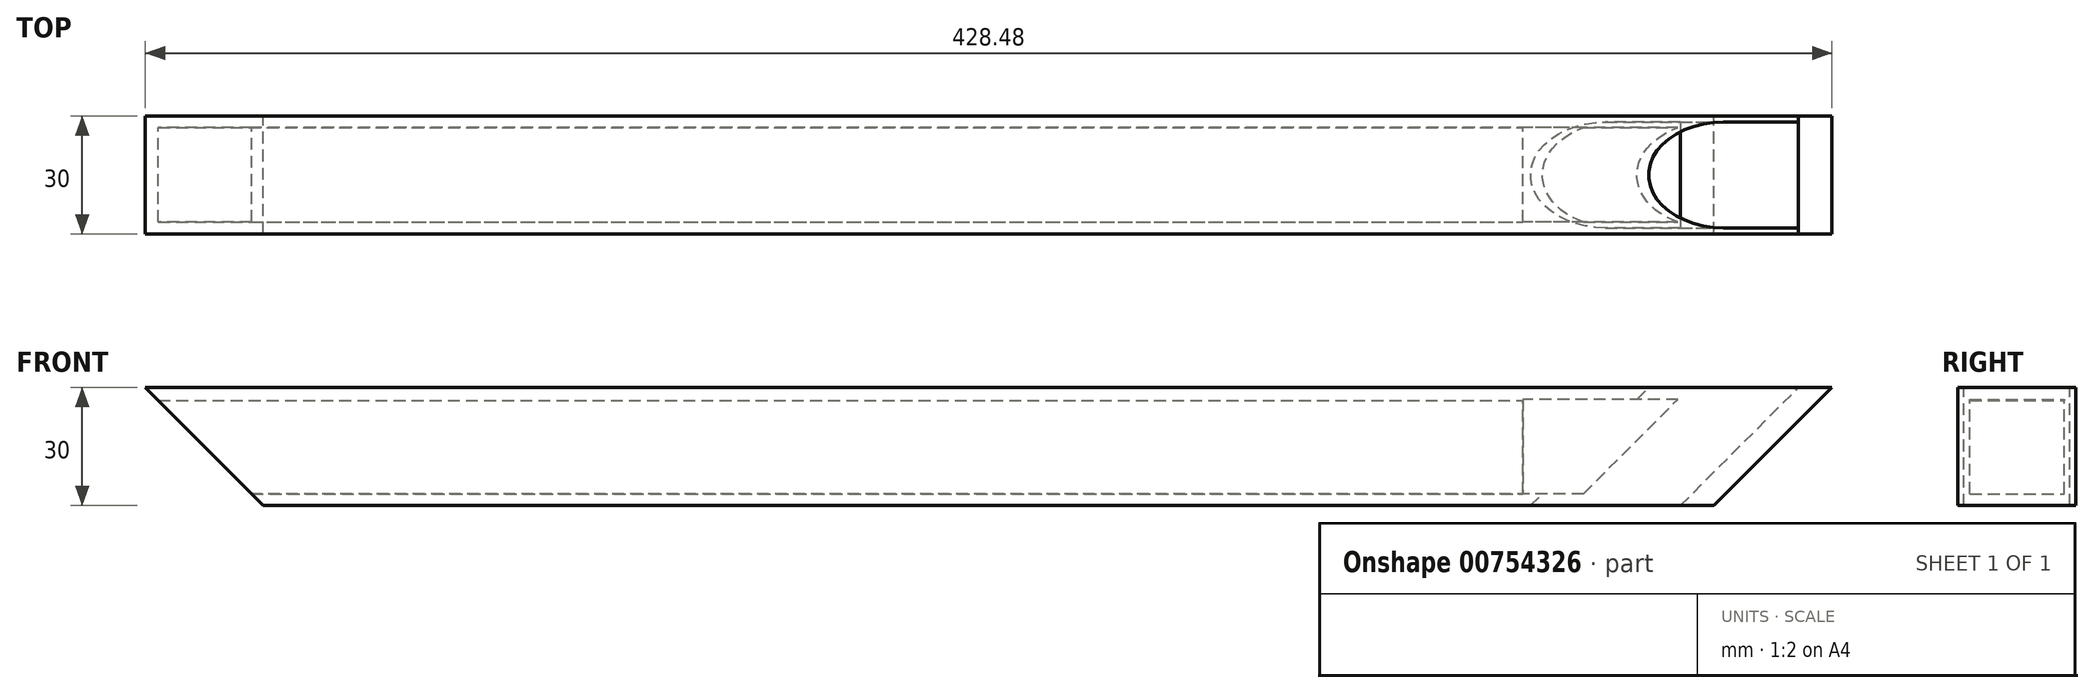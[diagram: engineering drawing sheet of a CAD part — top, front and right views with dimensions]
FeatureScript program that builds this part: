
annotation { "Feature Type Name" : "Feature", "Feature Type Description" : "" }
export const myFeature = defineFeature(function(context is Context, id is Id, definition is map)
    precondition{}
    {
        {
            var Q0;
            Q0=qCreatedBy(makeId("Right.planeOp"),FACE);
            var sketch = newSketch(context, id + "F0", { "sketchPlane" : qUnion([Q0])});
            skLineSegment(sketch, "E0.bottom", {"start": v(15, 15) * mm, "end": v(-15, 15) * mm});
            skLineSegment(sketch, "E0.top", {"start": v(15, -15) * mm, "end": v(-15, -15) * mm});
            skLineSegment(sketch, "E0.left", {"start": v(15, 15) * mm, "end": v(15, -15) * mm});
            skLineSegment(sketch, "E0.right", {"start": v(-15, 15) * mm, "end": v(-15, -15) * mm});
            skPoint(sketch, "E0.middle", {"position": v(0, 0) * mm});
            skLineSegment(sketch, "E1.bottom", {"start": v(12, -12) * mm, "end": v(-12, -12) * mm});
            skLineSegment(sketch, "E1.top", {"start": v(12, 12) * mm, "end": v(-12, 12) * mm});
            skLineSegment(sketch, "E1.left", {"start": v(12, -12) * mm, "end": v(12, 12) * mm});
            skLineSegment(sketch, "E1.right", {"start": v(-12, -12) * mm, "end": v(-12, 12) * mm});
            skLineSegment(sketch, "E2", {"start": v(12, 0) * mm, "end": v(15, 0) * mm, "construction": true});
            skLineSegment(sketch, "E3", {"start": v(0, 12) * mm, "end": v(0, 15) * mm, "construction": true});
            skSolve(sketch);
        }
        {
            var Q0;
            Q0=makeQuery(id+"F0.imprint","IMPRINT",FACE,{"disambiguationData":[TD([[makeQuery(id+"F0.imprint","IMPRINT",EDGE,{"derivedFrom":sQuery(id+"F0.wireOp",EDGE,"E0.bottom")}),1.0]])]});
            extrude(context, id + "F1", {"entities" : qUnion([Q0]), "depth" : 100 * mm, "offsetDistance" : 25 * mm});
        }
        {
            var Q0;
            Q0=makeQuery(id+"F1.opExtrude","SWEPT_FACE",FACE,{"disambiguationData":[OSD([sQuery(id+"F0.wireOp",EDGE,"E0.left")])]});
            var sketch = newSketch(context, id + "F2", { "sketchPlane" : qUnion([Q0])});
            skLineSegment(sketch, "E4", {"start": v(0, -15) * mm, "end": v(-30, -15) * mm, "construction": true});
            skLineSegment(sketch, "E5", {"start": v(-30, -15) * mm, "end": v(0, 15) * mm});
            skLineSegment(sketch, "E6", {"start": v(0, 15) * mm, "end": v(0, -15) * mm});
            skLineSegment(sketch, "E7", {"start": v(-30, -15) * mm, "end": v(0, -15) * mm});
            skSolve(sketch);
        }
        {
            var Q0;
            Q0=makeQuery(id+"F2.imprint","IMPRINT",FACE,{"disambiguationData":[TD([[makeQuery(id+"F2.imprint","IMPRINT",EDGE,{"derivedFrom":sQuery(id+"F2.wireOp",EDGE,"E5")}),-1.0]])]});
            extrude(context, id + "F3", {"entities" : qUnion([Q0]), "operationType" : NewBodyOperationType.REMOVE, "oppositeDirection" : true, "depth" : 30 * mm, "offsetDistance" : 25 * mm});
        }
        {
            var Q0;
            Q0=makeQuery(id+"F1.opExtrude","SWEPT_FACE",FACE,{"disambiguationData":[OSD([sQuery(id+"F0.wireOp",EDGE,"E0.right")])]});
            var sketch = newSketch(context, id + "F4", { "sketchPlane" : qUnion([Q0])});
            skLineSegment(sketch, "E8", {"start": v(100, -15) * mm, "end": v(70, -15) * mm});
            skLineSegment(sketch, "E9", {"start": v(70, -15) * mm, "end": v(100, 15) * mm});
            skLineSegment(sketch, "E10", {"start": v(100, 15) * mm, "end": v(100, -15) * mm});
            skSolve(sketch);
        }
        {
            var Q0;
            Q0 = qSketchRegion(id + "F4", true);
            extrude(context, id + "F5", {"entities" : qUnion([Q0]), "operationType" : NewBodyOperationType.REMOVE, "oppositeDirection" : true, "depth" : 30 * mm, "offsetDistance" : 25 * mm});
        }
        {
            var Q0;
            Q0=makeQuery(id+"F5.boolean.opBoolean","COPY",FACE,{"derivedFrom":makeQuery(id+"F5.opExtrude","SWEPT_FACE",FACE,{"disambiguationData":[OSD([sQuery(id+"F4.wireOp",EDGE,"E9")])]})});
            var sketch = newSketch(context, id + "F6", { "sketchPlane" : qUnion([Q0])});
            skLineSegment(sketch, "E11", {"start": v(12, 43.13) * mm, "end": v(15, 43.13) * mm, "construction": true});
            skLineSegment(sketch, "E12", {"start": v(-12, 43.13) * mm, "end": v(-15, 43.13) * mm, "construction": true});
            skLineSegment(sketch, "E13", {"start": v(15, 38.9) * mm, "end": v(15, 43.13) * mm});
            skLineSegment(sketch, "E14", {"start": v(-15, 43.13) * mm, "end": v(-15, 38.9) * mm});
            skLineSegment(sketch, "E15", {"start": v(-15, 38.9) * mm, "end": v(15, 38.9) * mm});
            skLineSegment(sketch, "E16", {"start": v(15, 43.13) * mm, "end": v(-15, 43.13) * mm});
            skSolve(sketch);
        }
        {
            var Q0;
            {var subQ4=sQuery(id+"F6.wireOp",EDGE,"E13");Q0=makeQuery(id+"F6.imprint","IMPRINT",FACE,{"disambiguationData":[TD([[makeQuery(id+"F6.imprint","IMPRINT",EDGE,{"derivedFrom":subQ4}),1.0]])]});}
            extrude(context, id + "F7", {"entities" : qUnion([Q0]), "operationType" : NewBodyOperationType.ADD, "depth" : 6 * mm, "offsetDistance" : 25 * mm});
        }
        {
            var Q0;
            Q0=makeQuery(id+"F7.opExtrude","SWEPT_FACE",FACE,{"disambiguationData":[OSD([sQuery(id+"F6.wireOp",EDGE,"E15")])]});
            var sketch = newSketch(context, id + "F8", { "sketchPlane" : qUnion([Q0])});
            skLineSegment(sketch, "E17", {"start": v(0, -60.1) * mm, "end": v(0, -46.65) * mm, "construction": true});
            skCircle(sketch, "E18", {"center": v(0, -46.65) * mm, "radius": 13.45 * mm});
            skLineSegment(sketch, "E19", {"start": v(0, -46.65) * mm, "end": v(15, -46.65) * mm, "construction": true});
            skLineSegment(sketch, "E20", {"start": v(0, -46.65) * mm, "end": v(-15, -46.65) * mm, "construction": true});
            skLineSegment(sketch, "E21", {"start": v(-13.45, -46.65) * mm, "end": v(-13.45, -60.1) * mm});
            skLineSegment(sketch, "E22", {"start": v(13.45, -46.65) * mm, "end": v(13.45, -60.1) * mm});
            skLineSegment(sketch, "E23", {"start": v(13.45, -60.1) * mm, "end": v(-13.45, -60.1) * mm});
            skSolve(sketch);
        }
        {
            var Q0;
            Q0 = qSketchRegion(id + "F8", true);
            extrude(context, id + "F9", {"entities" : qUnion([Q0]), "operationType" : NewBodyOperationType.REMOVE, "depth" : 100 * mm, "offsetDistance" : 25 * mm, "symmetric" : true});
        }
        {
            var Q0;
            Q0=makeQuery(id+"F7.boolean.opBoolean","MERGE",FACE,{"derivedFrom":[makeQuery(id+"F1.opExtrude","SWEPT_FACE",FACE,{"disambiguationData":[OSD([sQuery(id+"F0.wireOp",EDGE,"E0.left")])]}),makeQuery(id+"F7.opExtrude","SWEPT_FACE",FACE,{"disambiguationData":[OSD([sQuery(id+"F6.wireOp",EDGE,"E13")])]})]});
            var sketch = newSketch(context, id + "F10", { "sketchPlane" : qUnion([Q0])});
            skLineSegment(sketch, "E24", {"start": v(-30, -15) * mm, "end": v(-30, 15) * mm});
            skSolve(sketch);
        }
        {
            var Q0;
            Q0=sQuery(id+"F10.wireOp",EDGE,"E24");
            extrude(context, id + "F11", {"bodyType" : ToolBodyType.SURFACE, "surfaceEntities" : qUnion([Q0]), "oppositeDirection" : true, "depth" : 30 * mm, "offsetDistance" : 25 * mm});
        }
        {
            var Q0;
            Q0=makeQuery(id+"F11.opExtrude","SWEPT_FACE",FACE,{"disambiguationData":[OSD([sQuery(id+"F10.wireOp",EDGE,"E24")])]});
            var sketch = newSketch(context, id + "F12", { "sketchPlane" : qUnion([Q0])});
            skLineSegment(sketch, "E25.bottom", {"start": v(15, -15) * mm, "end": v(-15, -15) * mm});
            skLineSegment(sketch, "E25.top", {"start": v(15, 15) * mm, "end": v(-15, 15) * mm});
            skLineSegment(sketch, "E25.left", {"start": v(15, -15) * mm, "end": v(15, 15) * mm});
            skLineSegment(sketch, "E25.right", {"start": v(-15, -15) * mm, "end": v(-15, 15) * mm});
            skLineSegment(sketch, "E26.bottom", {"start": v(-11.96, -12) * mm, "end": v(12, -12) * mm});
            skLineSegment(sketch, "E26.top", {"start": v(-11.96, 11.7) * mm, "end": v(12, 11.7) * mm});
            skLineSegment(sketch, "E26.left", {"start": v(-11.96, -12) * mm, "end": v(-11.96, 11.7) * mm});
            skLineSegment(sketch, "E26.right", {"start": v(12, -12) * mm, "end": v(12, 11.7) * mm});
            skLineSegment(sketch, "E27", {"start": v(12, -10.15) * mm, "end": v(15, -10.15) * mm, "construction": true});
            skLineSegment(sketch, "E28", {"start": v(0, -12) * mm, "end": v(0, -15) * mm, "construction": true});
            skSolve(sketch);
        }
        {
            var Q0;
            Q0=makeQuery(id+"F7.boolean.opBoolean","MERGE",FACE,{"derivedFrom":[makeQuery(id+"F1.opExtrude","SWEPT_FACE",FACE,{"disambiguationData":[OSD([sQuery(id+"F0.wireOp",EDGE,"E0.left")])]}),makeQuery(id+"F7.opExtrude","SWEPT_FACE",FACE,{"disambiguationData":[OSD([sQuery(id+"F6.wireOp",EDGE,"E13")])]})]});
            var sketch = newSketch(context, id + "F13", { "sketchPlane" : qUnion([Q0])});
            skLineSegment(sketch, "E29.bottom", {"start": v(-30, -15) * mm, "end": v(0, -15) * mm});
            skLineSegment(sketch, "E29.top", {"start": v(-30, 15) * mm, "end": v(0, 15) * mm});
            skLineSegment(sketch, "E29.left", {"start": v(-30, -15) * mm, "end": v(-30, 15) * mm});
            skLineSegment(sketch, "E29.right", {"start": v(0, -15) * mm, "end": v(0, 15) * mm});
            skSolve(sketch);
        }
        {
            var Q0;
            Q0 = qSketchRegion(id + "F13", true);
            extrude(context, id + "F14", {"entities" : qUnion([Q0]), "operationType" : NewBodyOperationType.REMOVE, "oppositeDirection" : true, "depth" : 30 * mm, "offsetDistance" : 25 * mm});
        }
        {
            var Q0;
            Q0 = qSketchRegion(id + "F12", true);
            extrude(context, id + "F15", {"entities" : qUnion([Q0]), "operationType" : NewBodyOperationType.ADD, "oppositeDirection" : true, "depth" : 350 * mm, "offsetDistance" : 25 * mm});
        }
        {
            var Q0;
            Q0=makeQuery(id+"F15.opExtrude","CAP_EDGE",EDGE,{"disambiguationData":[OSD([sQuery(id+"F12.wireOp",EDGE,"E25.bottom")])],"isStart":false});
            chamfer(context, id + "F16", {"entities" : qUnion([Q0]), "width" : 30 * mm, "tangentPropagation" : true});
        }
        {
            var Q0;
            Q0=makeQuery(id+"F7.opExtrude","SWEPT_FACE",FACE,{"disambiguationData":[OSD([sQuery(id+"F6.wireOp",EDGE,"E16")])]});
            var sketch = newSketch(context, id + "F17", { "sketchPlane" : qUnion([Q0])});
            skLineSegment(sketch, "E30.bottom", {"start": v(-15, -60.1) * mm, "end": v(15, -60.1) * mm});
            skLineSegment(sketch, "E30.top", {"start": v(-15, -66.1) * mm, "end": v(15, -66.1) * mm});
            skLineSegment(sketch, "E30.left", {"start": v(-15, -60.1) * mm, "end": v(-15, -66.1) * mm});
            skLineSegment(sketch, "E30.right", {"start": v(15, -60.1) * mm, "end": v(15, -66.1) * mm});
            skSolve(sketch);
        }
        {
            var Q0;
            Q0=makeQuery(id+"F17.imprint","IMPRINT",FACE,{"disambiguationData":[TD([[makeQuery(id+"F17.imprint","IMPRINT",EDGE,{"derivedFrom":sQuery(id+"F17.wireOp",EDGE,"E30.top")}),-1.0]])]});
            extrude(context, id + "F18", {"entities" : qUnion([Q0]), "operationType" : NewBodyOperationType.ADD, "depth" : 44.18 * mm, "offsetDistance" : 25 * mm});
        }
        {
            var Q0;
            Q0=makeQuery(id+"F18.opExtrude","CAP_EDGE",EDGE,{"disambiguationData":[OSD([sQuery(id+"F17.wireOp",EDGE,"E30.bottom")])],"isStart":false});
            chamfer(context, id + "F19", {"entities" : qUnion([Q0]), "width" : 6 * mm, "tangentPropagation" : true});
        }
        {
            var Q0;
            Q0=makeQuery(id+"F7.opExtrude","CAP_EDGE",EDGE,{"disambiguationData":[OSD([sQuery(id+"F6.wireOp",EDGE,"E15")])],"isStart":false});
            chamfer(context, id + "F20", {"entities" : qUnion([Q0]), "width" : 6 * mm, "tangentPropagation" : true});
        }
    });
